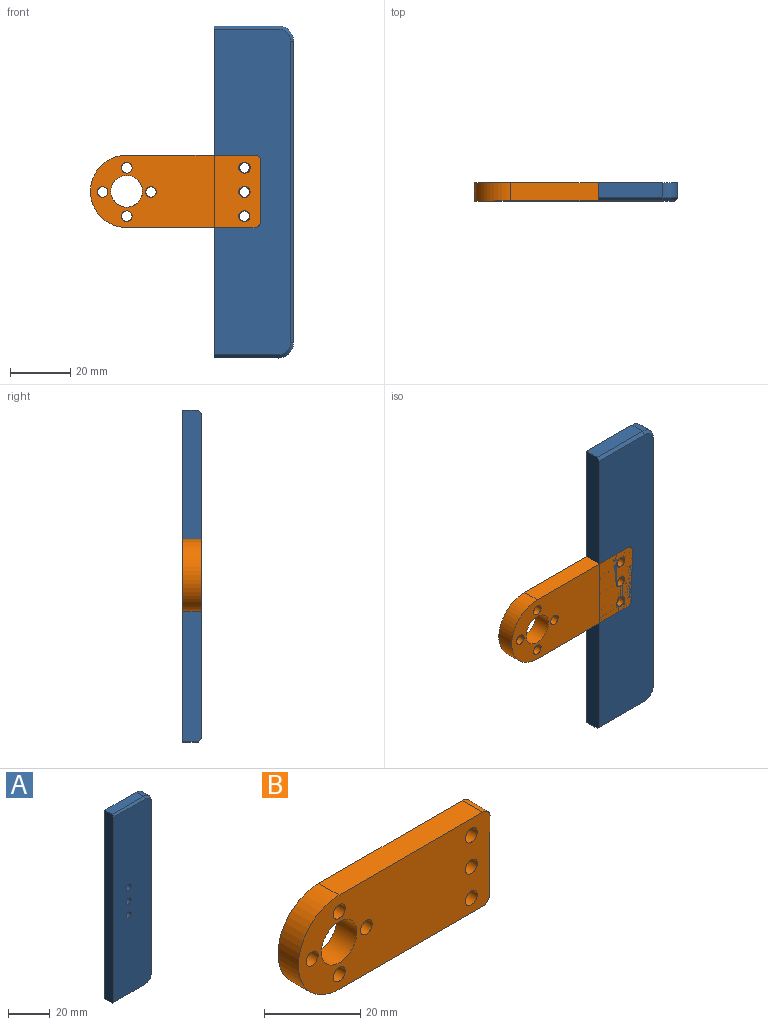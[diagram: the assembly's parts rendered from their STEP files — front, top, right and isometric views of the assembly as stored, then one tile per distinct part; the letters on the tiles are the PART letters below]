
ASSEMBLY  parts=2 mates=1
PART A: 16 faces, bbox 26.3x6x110 mm
  f0: plane 21.22x5mm, normal (0,0,1), area 106.1mm2, adj f1,f7,f10,f15
  f1: plane 110x6mm, normal (-1,0,0), area 659mm2, adj f0,f2,f9,f10,f11,f15
  f2: plane 21.22x5mm, normal (0,0,-1), area 106.1mm2, adj f1,f3,f10,f11
  f3: cylinder r=5mm len=5mm, axis (0,1,0), area 39.3mm2, adj f2,f4,f10,f12
  f4: plane 100x5mm, normal (1,0,0), area 500mm2, adj f3,f7,f10,f13
  f5: cylinder r=1.75mm len=6mm, axis (0,1,0), area 66mm2, adj f9,f10
  f6: cylinder r=1.75mm len=6mm, axis (0,1,0), area 66mm2, adj f9,f10
  f7: cylinder r=5mm len=5mm, axis (0,1,0), area 39.3mm2, adj f0,f4,f10,f14
  f8: cylinder r=1.75mm len=6mm, axis (0,1,0), area 66mm2, adj f9,f10
  f9: plane 108.01x25.25mm, normal (0,-1,0), area 2688.5mm2, adj f1,f5,f6,f8,f11,f12,f13,f14
  f10: plane 110.01x26.25mm, normal (0,1,0), area 2845.1mm2, adj f0,f1,f2,f3,f4,f5,f6,f7
  f11: plane 21.23x1.01mm, normal (0,-0.71,-0.71), area 30mm2, adj f1,f2,f9,f12
  f12: cone r=4mm half-angle=45deg, axis (0,1,0), area 10mm2, adj f3,f9,f11,f13
  f13: plane 100x1.03mm, normal (0.71,-0.71,0), area 141.4mm2, adj f4,f9,f12,f14
  f14: cone r=4mm half-angle=45deg, axis (0,1,0), area 10mm2, adj f7,f9,f13,f15
  f15: plane 21.23x1.01mm, normal (0,-0.71,0.71), area 30mm2, adj f0,f1,f9,f14
PART B: 16 faces, bbox 56.4x6x24 mm
  f0: cylinder r=2mm len=6mm, axis (0,1,0), area 17.7mm2, adj f1,f5,f6,f7
  f1: plane 19.99x6mm, normal (1,0,-0.01), area 119.9mm2, adj f0,f2,f6,f7
  f2: cylinder r=2mm len=6mm, axis (0,1,0), area 19.8mm2, adj f1,f3,f6,f7
  f3: plane 42.3x6mm, normal (0,0,1), area 253.8mm2, adj f2,f4,f6,f7
  f4: cylinder r=11.99mm len=23.98mm, axis (0,1,0), area 226mm2, adj f3,f5,f6,f7
  f5: plane 42.53x6mm, normal (0,0,-1), area 255.2mm2, adj f0,f4,f6,f7
  f6: plane 56.43x23.99mm, normal (0,-1,0), area 1134.9mm2, adj f0,f1,f2,f3,f4,f5,f8,f9
  f7: plane 56.43x23.99mm, normal (0,1,0), area 1134.9mm2, adj f0,f1,f2,f3,f4,f5,f8,f9
  f8: cylinder r=5.25mm len=10.5mm, axis (0,1,0), area 197.9mm2, adj f6,f7
  f9: cylinder r=1.75mm len=6mm, axis (0,1,0), area 66mm2, adj f6,f7
  f10: cylinder r=1.75mm len=6mm, axis (0,1,0), area 66mm2, adj f6,f7
  f11: cylinder r=1.75mm len=6mm, axis (0,1,0), area 66mm2, adj f6,f7
  f12: cylinder r=1.75mm len=6mm, axis (0,1,0), area 66mm2, adj f6,f7
  f13: cylinder r=1.75mm len=6mm, axis (0,1,0), area 66mm2, adj f6,f7
  f14: cylinder r=1.75mm len=6mm, axis (0,1,0), area 66mm2, adj f6,f7
  f15: cylinder r=1.75mm len=6mm, axis (0,1,0), area 66mm2, adj f6,f7
PLACE A t=(22.57,-0.53,22.55)mm
PLACE B t=(50.03,-0.53,25.61)mm
MATE pin_slot B.f14 <-> A.f5  axis (0,-1,0) through (70.73,-6.53,24.98)mm
